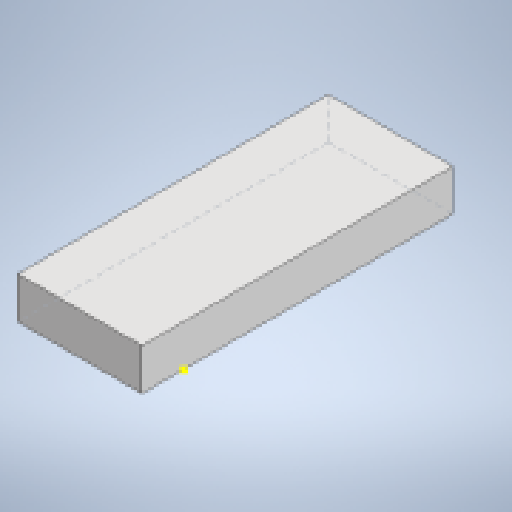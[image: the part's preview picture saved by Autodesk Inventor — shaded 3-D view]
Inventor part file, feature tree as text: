
AUTODESK INVENTOR PART (.ipt)
format: ipt  version: 2023 (Build 270158000, 158)  size: 129,024 bytes
history: native  units: mm
features: sketch x2, extrude x1
ambient origin geometry x8: Origin, YZ Plane, XZ Plane, XY Plane, X Axis, Y Axis, Z Axis, Center Point
bodies: Solid1 (feature_tree)
feature tree (3):
  extrude  "Extrusion1"  Depth=150.0mm
  sketch  "Sketch2"  dims[d2=20.0mm d3=20.0mm d4=150.0mm d5=150.0mm d6=20.0mm d7=0.0mm]
  sketch  "Sketch1"  dims[d0=100.0mm d1=150.0mm]
